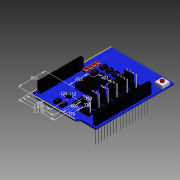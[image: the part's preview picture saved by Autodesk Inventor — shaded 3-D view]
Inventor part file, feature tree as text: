
AUTODESK INVENTOR PART (.ipt)
format: ipt  version: 2013 (Build 170138000, 138)  size: 2,237,440 bytes
history: native  units: in
note: dims shown in document units (in); Inventor stores cm internally (conversion verified against a paired STEP export)
features: projected_geometry x41, extrude x14, sketch x9, fillet x2, chamfer x1
ambient origin geometry x8: Origin, YZ Plane, XZ Plane, XY Plane, X Axis, Y Axis, Z Axis, Center Point
bodies: Solid1 (feature_tree)
feature tree (67):
  extrude  "PCB BD"  Depth=2.6in
  extrude  "SK14 GP"  Depth=0.08in
  extrude  "DET1"  Depth=0.09in
  extrude  "Extrusion4"  Depth=0.06in TaperAngle=0.0deg
  extrude  "Extrusion5"  Depth=0.1825in
  fillet  "Fillet1"  Radius=0.105in
  chamfer  "Chamfer1"  Distance=0.09in
  sketch  "Sketch6"  dims[d9=0.1in d10=0.1825in d11=0.105in]
  extrude  "Extrusion6"  Depth=0.09in
  extrude  "Extrusion7"  Depth=0.09in
  extrude  "Extrusion8"  Depth=0.12in
  extrude  "Extrusion9"  Depth=0.07in TaperAngle=0.0deg
  fillet  "Fillet2"  Radius=0.018in
  extrude  "Extrusion10"  Depth=0.065in
  extrude  "Extrusion11"  Depth=0.018in
  sketch  "Sketch10"  dims[d16=0.95in d17=0.09in d18=0.09in d19=0.09in d20=0.12in d21=0.07in d22=0.0in d23=0.018in d24=0.065in d25=0.018in d26=0.065in d27=0.018in d28=0.018in d29=0.018in d30=0.0252in d31=0.065in d32=0.01in d33=0.0in d34=0.1in d36=0.8in d37=0.05in d38=0.05in d39=1.0in d40=0.045in d42=0.03in d44=0.05in d46=0.05in d47=3.937in d49=0.1in d50=0.3937in d52=1.0in d54=0.05in d55=3.1496in d57=0.1in d58=0.3937in d60=1.0in d62=0.035in d63=0.035in d64=0.1in d65=0.6in d66=0.03in d68=0.035in d69=0.05in d70=2.3622in d72=0.1in d73=0.3937in d75=1.0in d77=0.8in d78=0.045in d79=0.03in d81=0.035in d82=3.1496in d84=0.1in d85=0.3937in d87=1.0in d89=0.34in d90=0.0in d91=0.575in d92=0.0in d93=0.0156in d94=0.0075in d95=0.125in d96=45.0deg d97=0.225in d99=0.3in d100=0.2in d101=0.295in d102=0.192in d103=0.054in d104=0.035in d105=1.5748in d107=0.297in d108=0.3937in d110=1.0in d112=0.4in d113=0.05in d116=0.07in d117=0.225in d118=0.295in d119=0.035in d120=0.0525in d121=0.7874in d123=0.3in d124=0.3937in d126=1.0in d128=0.025in d129=0.035in d130=0.113in d131=0.15in d132=0.15in d133=1.5748in d135=0.297in d136=0.3937in d138=1.0in d141=0.035in d142=0.113in d143=0.035in d146=0.0765in d147=0.0765in d148=0.077in d149=0.7874in d151=0.297in d152=0.3937in d154=1.0in d156=0.05in d157=0.0in d158=0.456in d159=0.0in d160=0.44in d161=0.0in d162=0.135in d163=0.098in d164=0.23in d166=1.5in d167=1.5748in d169=0.13in d170=0.3937in d172=1.0in d174=0.075in d175=0.0in d176=0.0156in d177=0.25in d178=0.25in d179=0.125in d180=0.01in d181=0.0965in d182=0.0in d183=0.12in d184=0.045in d185=0.0in d186=0.121in d188=0.112in d189=0.6in d190=0.805in d191=0.379in d192=0.338in d193=0.15in d194=1.175in d195=0.621in d196=0.427in d197=0.892in d198=1.025in d199=0.14in d200=0.0in d201=0.069in d202=0.0in d203=0.039in d204=0.0in]
  extrude  "Extrusion12"  Depth=0.065in
  extrude  "Extrusion13"  Depth=0.018in
  extrude  "Extrusion14"  Depth=0.018in
  sketch  "Sketch1"  dims[d0=2.1in d1=2.6in]
  sketch  "Sketch2"  dims[d2=2.6in d3=0.08in]
  projected_geometry  "Projected Loop1"
  projected_geometry  "Projected Loop2"
  projected_geometry  "Projected Loop3"
  projected_geometry  "Projected Loop4"
  projected_geometry  "Projected Loop5"
  projected_geometry  "Projected Loop6"
  projected_geometry  "Projected Loop7"
  projected_geometry  "Projected Loop8"
  projected_geometry  "Projected Loop9"
  sketch  "Sketch4"  dims[d4=0.5in d5=0.09in]
  sketch  "Sketch5"  dims[d6=1.315in d7=0.06in d8=0.0in]
  projected_geometry  "Projected Loop10"
  projected_geometry  "Projected Loop11"
  projected_geometry  "Projected Loop12"
  projected_geometry  "Projected Loop13"
  projected_geometry  "Projected Loop14"
  projected_geometry  "Projected Loop15"
  projected_geometry  "Projected Loop16"
  projected_geometry  "Projected Loop17"
  projected_geometry  "Projected Loop18"
  projected_geometry  "Projected Loop19"
  projected_geometry  "Projected Loop20"
  projected_geometry  "Projected Loop21"
  projected_geometry  "Projected Loop22"
  projected_geometry  "Projected Loop23"
  projected_geometry  "Projected Loop24"
  projected_geometry  "Projected Loop25"
  projected_geometry  "Projected Loop26"
  projected_geometry  "Projected Loop27"
  projected_geometry  "Projected Loop28"
  projected_geometry  "Projected Loop29"
  projected_geometry  "Projected Loop30"
  projected_geometry  "Projected Loop31"
  projected_geometry  "Projected Loop32"
  projected_geometry  "Projected Loop33"
  projected_geometry  "Projected Loop34"
  projected_geometry  "Projected Loop35"
  projected_geometry  "Projected Loop36"
  projected_geometry  "Projected Loop37"
  projected_geometry  "Projected Loop38"
  projected_geometry  "Projected Loop39"
  projected_geometry  "Projected Loop40"
  projected_geometry  "Projected Loop41"
  sketch  "Sketch7"  dims[d13=1.1375in]
  sketch  "Sketch8"  dims[d14=0.09in]
  sketch  "Sketch9"  dims[d15=0.6615in]
